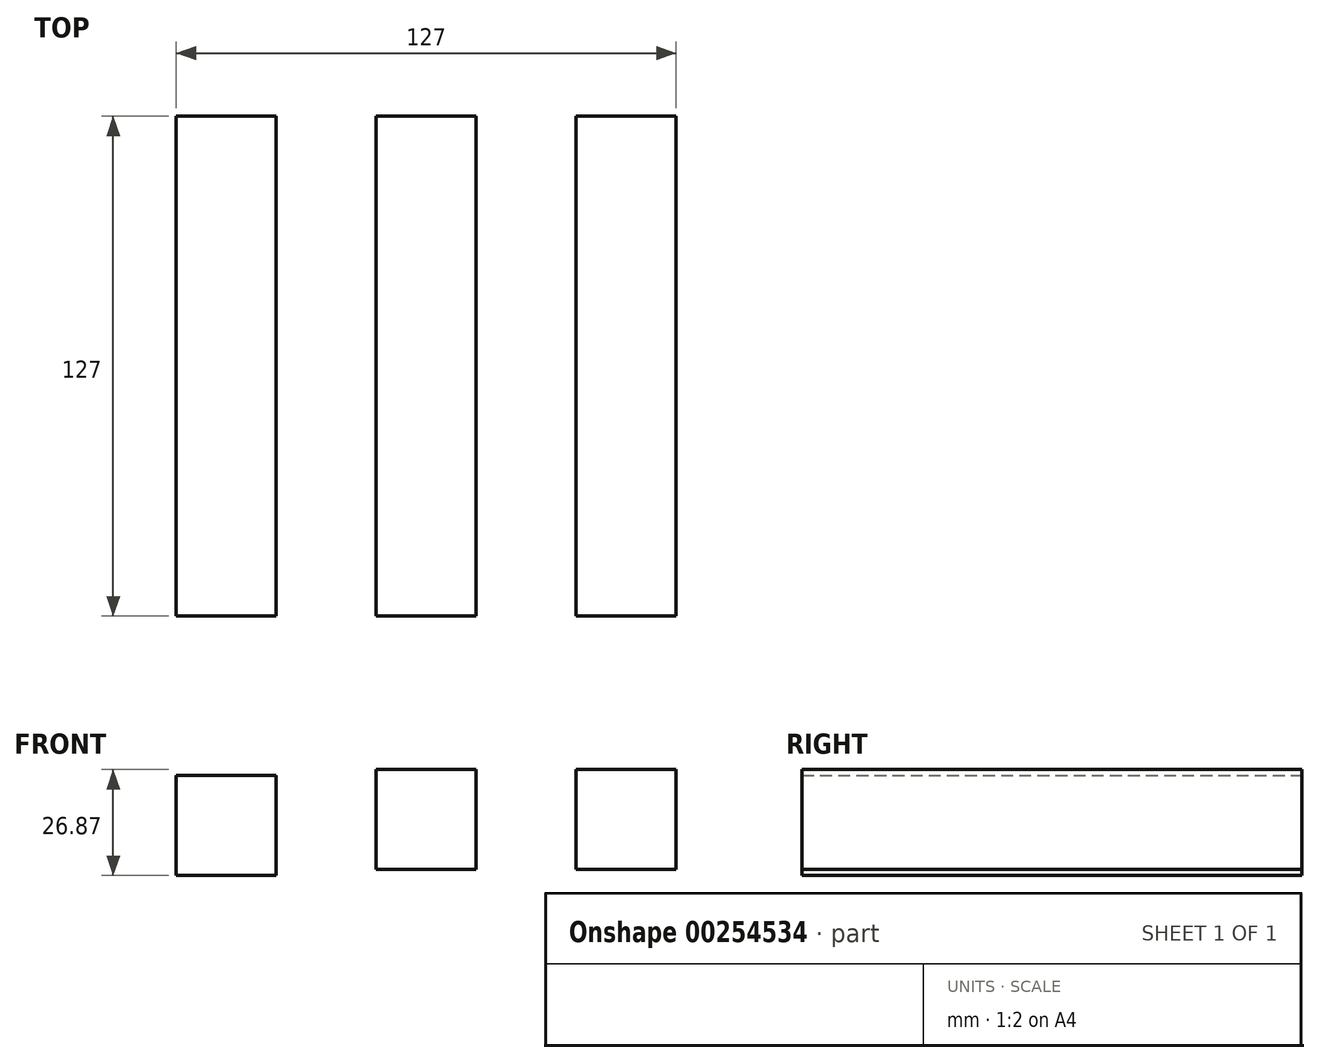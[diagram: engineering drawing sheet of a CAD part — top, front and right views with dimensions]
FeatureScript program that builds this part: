
annotation { "Feature Type Name" : "Feature", "Feature Type Description" : "" }
export const myFeature = defineFeature(function(context is Context, id is Id, definition is map)
    precondition{}
    {
        {
            var Q0;
            Q0=qCreatedBy(makeId("Front.planeOp"),FACE);
            var sketch = newSketch(context, id + "F0", { "sketchPlane" : qUnion([Q0])});
            skLineSegment(sketch, "E0.bottom", {"start": v(12.7, 12.7) * mm, "end": v(-12.7, 12.7) * mm});
            skLineSegment(sketch, "E0.top", {"start": v(12.7, -12.7) * mm, "end": v(-12.7, -12.7) * mm});
            skLineSegment(sketch, "E0.left", {"start": v(12.7, 12.7) * mm, "end": v(12.7, -12.7) * mm});
            skLineSegment(sketch, "E0.right", {"start": v(-12.7, 12.7) * mm, "end": v(-12.7, -12.7) * mm});
            skPoint(sketch, "E0.middle", {"position": v(0, 0) * mm});
            skLineSegment(sketch, "E1", {"start": v(0, 0) * mm, "end": v(-50.8, 0) * mm});
            skLineSegment(sketch, "E2", {"start": v(0, 0) * mm, "end": v(50.8, 0) * mm});
            skLineSegment(sketch, "E3.bottom", {"start": v(-38.1, 11.23) * mm, "end": v(-63.5, 11.23) * mm});
            skLineSegment(sketch, "E3.top", {"start": v(-38.1, -14.17) * mm, "end": v(-63.5, -14.17) * mm});
            skLineSegment(sketch, "E3.left", {"start": v(-38.1, 11.23) * mm, "end": v(-38.1, -14.17) * mm});
            skLineSegment(sketch, "E3.right", {"start": v(-63.5, 11.23) * mm, "end": v(-63.5, -14.17) * mm});
            skPoint(sketch, "E3.middle", {"position": v(-50.8, -1.47) * mm});
            skLineSegment(sketch, "E4.bottom", {"start": v(63.5, 12.7) * mm, "end": v(38.1, 12.7) * mm});
            skLineSegment(sketch, "E4.top", {"start": v(63.5, -12.7) * mm, "end": v(38.1, -12.7) * mm});
            skLineSegment(sketch, "E4.left", {"start": v(63.5, 12.7) * mm, "end": v(63.5, -12.7) * mm});
            skLineSegment(sketch, "E4.right", {"start": v(38.1, 12.7) * mm, "end": v(38.1, -12.7) * mm});
            skPoint(sketch, "E4.middle", {"position": v(50.8, 0) * mm});
            skSolve(sketch);
        }
        {
            var Q0;
            {var subQ3=sQuery(id+"F0.wireOp",EDGE,"E3.bottom");Q0=makeQuery(id+"F0.imprint","IMPRINT",FACE,{"disambiguationData":[TD([[makeQuery(id+"F0.imprint","IMPRINT",EDGE,{"derivedFrom":subQ3}),1.0]])]});}
            extrude(context, id + "F1", {"entities" : qUnion([Q0]), "endBound" : BoundingType.SYMMETRIC, "depth" : 127 * mm});
        }
        {
            var Q0;
            {var subQ5=sQuery(id+"F0.wireOp",EDGE,"E0.bottom");Q0=makeQuery(id+"F0.imprint","IMPRINT",FACE,{"disambiguationData":[TD([[makeQuery(id+"F0.imprint","IMPRINT",EDGE,{"derivedFrom":subQ5}),1.0]])]});}
            var Q1;
            {var subQ5=sQuery(id+"F0.wireOp",EDGE,"E0.top");Q1=makeQuery(id+"F0.imprint","IMPRINT",FACE,{"disambiguationData":[TD([[makeQuery(id+"F0.imprint","IMPRINT",EDGE,{"derivedFrom":subQ5}),-1.0]])]});}
            extrude(context, id + "F2", {"entities" : qUnion([Q0, Q1]), "endBound" : BoundingType.SYMMETRIC, "depth" : 127 * mm});
        }
        {
            var Q0;
            {var subQ1=sQuery(id+"F0.wireOp",EDGE,"E4.bottom");Q0=makeQuery(id+"F0.imprint","IMPRINT",FACE,{"disambiguationData":[TD([[makeQuery(id+"F0.imprint","IMPRINT",EDGE,{"derivedFrom":subQ1}),1.0]])]});}
            extrude(context, id + "F3", {"entities" : qUnion([Q0]), "endBound" : BoundingType.SYMMETRIC, "depth" : 127 * mm});
        }
    });
